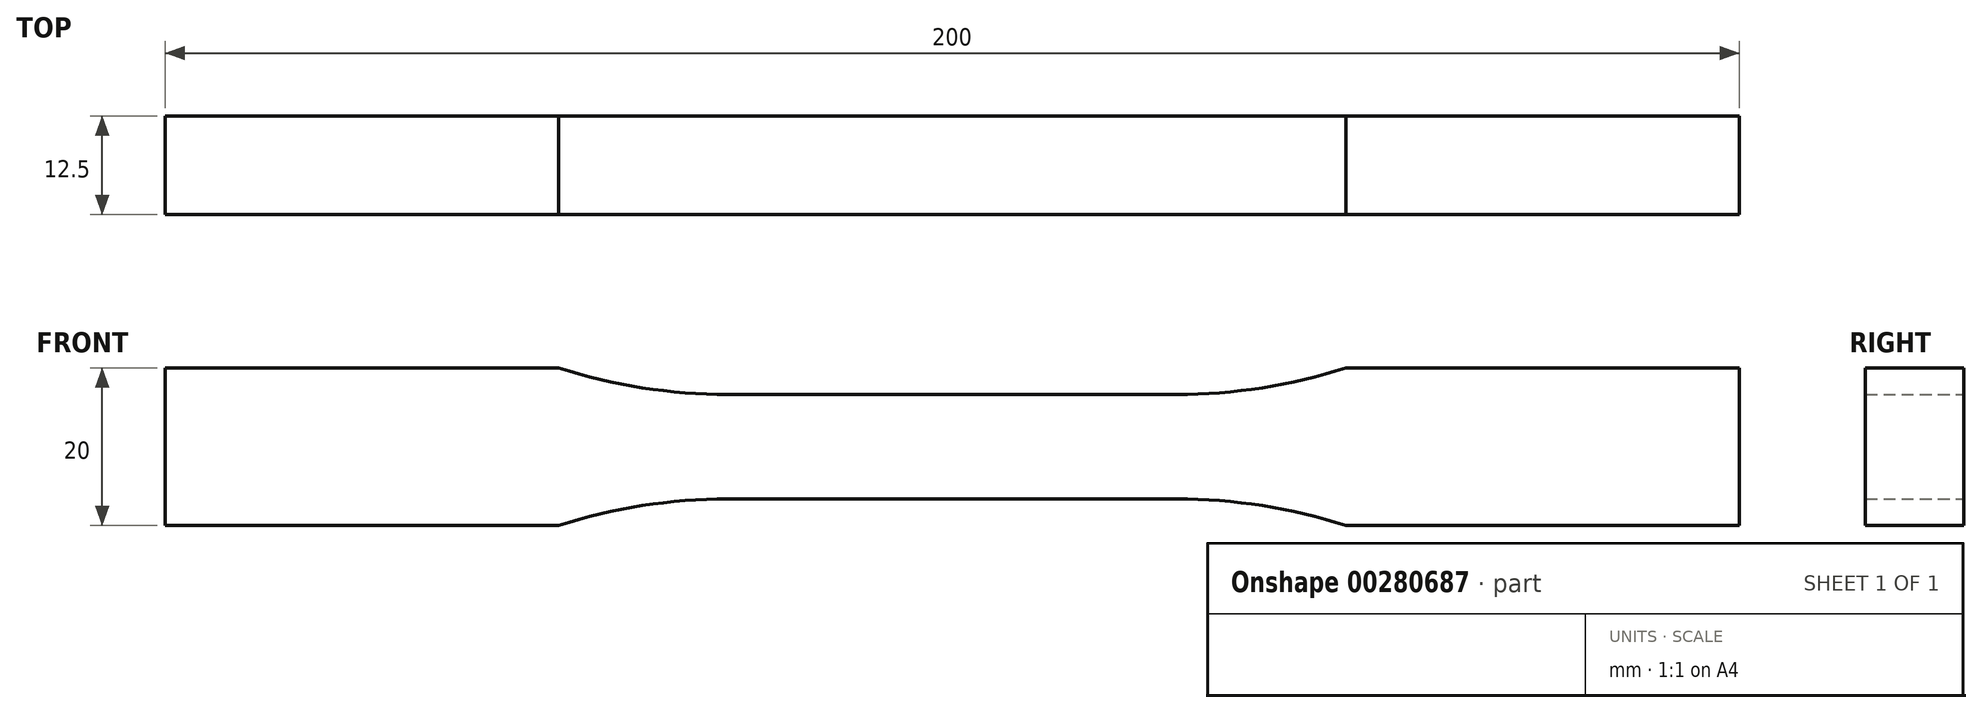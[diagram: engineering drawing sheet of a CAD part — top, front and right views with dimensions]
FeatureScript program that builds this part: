
annotation { "Feature Type Name" : "Feature", "Feature Type Description" : "" }
export const myFeature = defineFeature(function(context is Context, id is Id, definition is map)
    precondition{}
    {
        {
            var Q0;
            Q0=qCreatedBy(makeId("Front.planeOp"),FACE);
            var sketch = newSketch(context, id + "F0", { "sketchPlane" : qUnion([Q0])});
            skLineSegment(sketch, "E0", {"start": v(0, 6.64) * mm, "end": v(28.5, 6.64) * mm});
            skArc(sketch, "E1", {"start": v(28.5, 6.64) * mm, "mid": v(39.38, 7.49) * mm, "end": v(50, 10) * mm});
            skLineSegment(sketch, "E2", {"start": v(50, 10) * mm, "end": v(100, 10) * mm});
            skLineSegment(sketch, "E3", {"start": v(100, 10) * mm, "end": v(100, 0) * mm});
            skLineSegment(sketch, "E4.MirrorCS", {"start": v(0, -6.64) * mm, "end": v(28.5, -6.64) * mm});
            skLineSegment(sketch, "E5.MirrorCS", {"start": v(100, -10) * mm, "end": v(100, 0) * mm});
            skLineSegment(sketch, "E6.MirrorCS", {"start": v(50, -10) * mm, "end": v(100, -10) * mm});
            skArc(sketch, "E7.MirrorCS", {"start": v(28.5, -6.64) * mm, "mid": v(39.38, -7.49) * mm, "end": v(50, -10) * mm});
            skArc(sketch, "E8.MirrorCS", {"start": v(-28.5, -6.64) * mm, "mid": v(-39.38, -7.49) * mm, "end": v(-50, -10) * mm});
            skLineSegment(sketch, "E9.MirrorCS", {"start": v(-50, -10) * mm, "end": v(-100, -10) * mm});
            skArc(sketch, "E10.MirrorCS", {"start": v(-28.5, 6.64) * mm, "mid": v(-39.38, 7.49) * mm, "end": v(-50, 10) * mm});
            skLineSegment(sketch, "E11.MirrorCS", {"start": v(-50, 10) * mm, "end": v(-100, 10) * mm});
            skLineSegment(sketch, "E12.MirrorCS", {"start": v(-100, -10) * mm, "end": v(-100, 0) * mm});
            skLineSegment(sketch, "E13.MirrorCS", {"start": v(0, -6.64) * mm, "end": v(-28.5, -6.64) * mm});
            skLineSegment(sketch, "E14.MirrorCS", {"start": v(-100, 10) * mm, "end": v(-100, 0) * mm});
            skLineSegment(sketch, "E15.MirrorCS", {"start": v(0, 6.64) * mm, "end": v(-28.5, 6.64) * mm});
            skSolve(sketch);
        }
        {
            var Q0;
            Q0 = qSketchRegion(id + "F0", true);
            extrude(context, id + "F1", {"entities" : qUnion([Q0]), "endBound" : BoundingType.SYMMETRIC, "depth" : 12.5 * mm});
        }
    });
